# Revit family: Dynamic Fenestration - Pivot Door In Swing No Sill
name_source: partatom
category: Doors
units: mm (PartAtom-declared; Revit-internal decimal feet)

## family parameters
Always vertical = Yes
Cut with Voids When Loaded = No
Host = Wall
OmniClass Number = 23.30.20.00
OmniClass Title = Windows
Room Calculation Point = No
Shared = No

## types (1)
- 84" x 132"
    Analytic Construction = <None>
    Default Sill Height = 254 mm  [stored 0.833333 ft]
    Define Thermal Properties by = Schematic Type
    Description = Pivot Door In Swing No Sill
    Frame Material = Arte Metal
    Gap Fill = Argon
    Glass Material = Glass
    Glass Type = Triple Silve LowE / Clear
    Handle Height = 914 mm
    Height = 3267 mm
    Manufacturer = Dynamic Fenestration
    Max. Height = 3353 mm
    Max. Width = 2134 mm
    Min. Height = 1803 mm
    Min. Width = 610 mm
    Model = Door
    Rough Height = 3353 mm
    Rough Width = 2134 mm
    Rubber Material = Rubber
    Thickness = 68 mm
    Wall Closure = By host
    Width = 2048 mm

note: [stored X ft] marks values corroborated as IEEE doubles in the binary element streams (Revit-internal decimal feet)

## geometry (parser evidence)
native form markers: Sweep x20
no freeform markers — native parametric forms only
